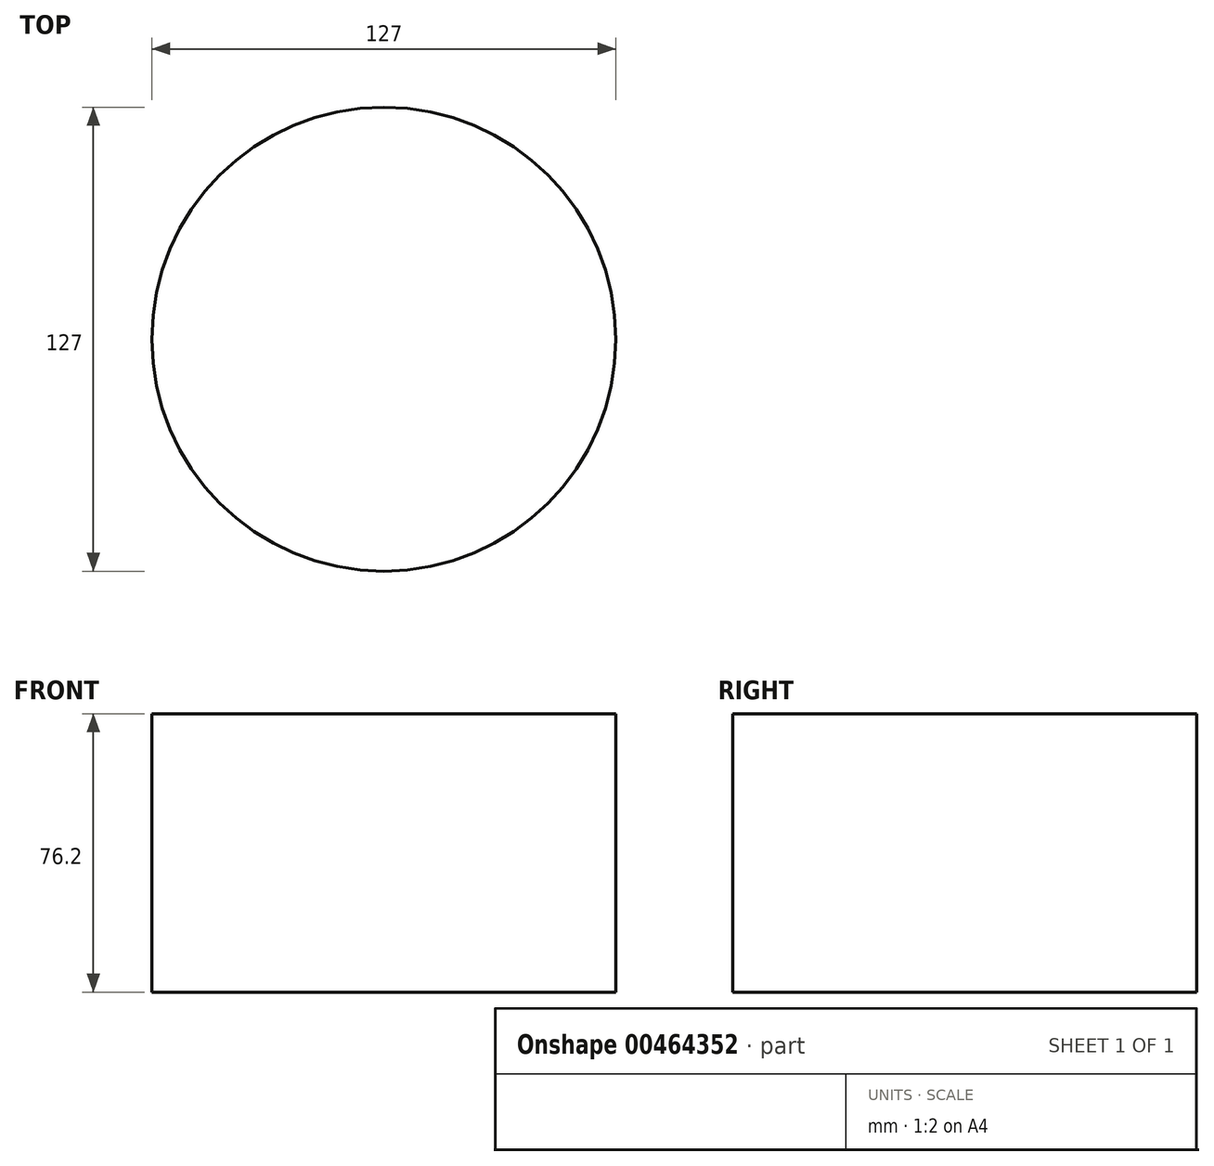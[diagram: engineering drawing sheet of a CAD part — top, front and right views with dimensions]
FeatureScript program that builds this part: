
annotation { "Feature Type Name" : "Feature", "Feature Type Description" : "" }
export const myFeature = defineFeature(function(context is Context, id is Id, definition is map)
    precondition{}
    {
        {
            var Q0;
            Q0=qCreatedBy(makeId("Top.planeOp"),FACE);
            var sketch = newSketch(context, id + "F0", { "sketchPlane" : qUnion([Q0])});
            skCircle(sketch, "E0", {"center": v(0, 0) * mm, "radius": 63.5 * mm});
            skSolve(sketch);
        }
        {
            var Q0;
            Q0=makeQuery(id+"F0.imprint","IMPRINT",FACE,{"disambiguationData":[TD([[makeQuery(id+"F0.imprint","IMPRINT",EDGE,{"derivedFrom":sQuery(id+"F0.wireOp",EDGE,"E0")}),1.0]])]});
            extrude(context, id + "F1", {"entities" : qUnion([Q0]), "depth" : 76.2 * mm});
        }
    });
